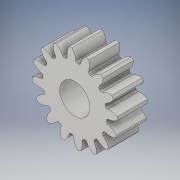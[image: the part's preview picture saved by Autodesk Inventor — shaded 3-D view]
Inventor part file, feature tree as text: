
AUTODESK INVENTOR PART (.ipt)
format: ipt  version: 2019 (Build 230136000, 136)  size: 363,520 bytes
history: native  units: in
note: dims shown in document units (in); Inventor stores cm internally (conversion verified against a paired STEP export)
features: extrude x2, sketch x2, projected_geometry x1, other x1
ambient origin geometry x8: Origin, YZ Plane, XZ Plane, XY Plane, X Axis, Y Axis, Z Axis, Center Point
bodies: Solid1 (feature_tree)
feature tree (6):
  extrude  "Extrusion1"  Depth=0.1979in
  extrude  "Extrusion2"  [1 undecoded]
  sketch  "Sketch1"  dims[d0=0.14in d1=0.0in d2=0.1979in]
  projected_geometry  "Projected Loop1"
  sketch  "Sketch2"  dims[d3=1.0in d4=0.0in]
  other  "bore"
note: 1 required parameter value undecoded (feature->parameter linkage not recoverable at this tier; creation-order binding heuristic only, values carry confidence <= 0.55)
